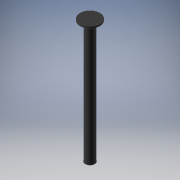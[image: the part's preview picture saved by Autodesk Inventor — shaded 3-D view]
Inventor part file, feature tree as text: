
AUTODESK INVENTOR PART (.ipt)
format: ipt  version: 2018 (Build 220112000, 112)  size: 93,184 bytes
history: native  units: in
note: dims shown in document units (in); Inventor stores cm internally (conversion verified against a paired STEP export)
features: extrude x2, sketch x2
ambient origin geometry x8: Origin, YZ Plane, XZ Plane, XY Plane, X Axis, Y Axis, Z Axis, Center Point
bodies: Solid1 (feature_tree)
feature tree (4):
  extrude  "Extrusion1"  Depth=3.3071in TaperAngle=0.0deg
  extrude  "Extrusion2"  Depth=0.0409in TaperAngle=0.0deg
  sketch  "Sketch1"  dims[d0=0.252in d1=3.3071in d2=0.0in]
  sketch  "Sketch2"  dims[d3=0.5315in d4=0.0409in d5=0.0in]
